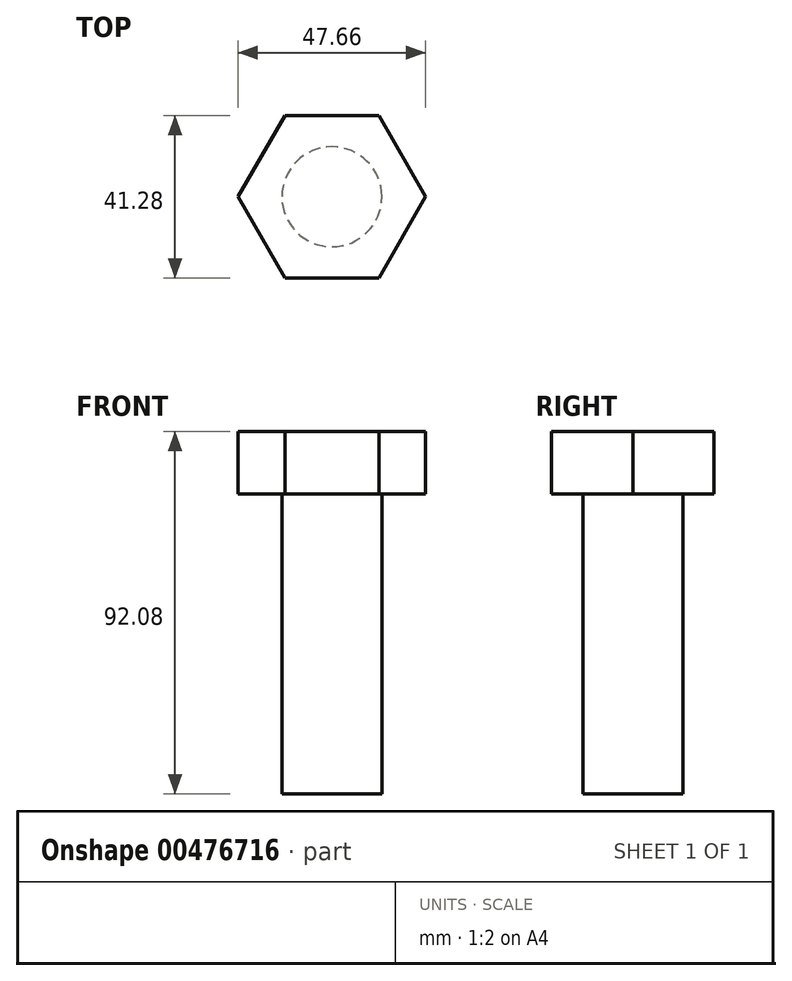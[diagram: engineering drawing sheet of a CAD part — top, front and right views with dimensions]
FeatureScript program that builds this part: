
annotation { "Feature Type Name" : "Feature", "Feature Type Description" : "" }
export const myFeature = defineFeature(function(context is Context, id is Id, definition is map)
    precondition{}
    {
        {
            var Q0;
            Q0=qCreatedBy(makeId("Top.planeOp"),FACE);
            var sketch = newSketch(context, id + "F0", { "sketchPlane" : qUnion([Q0])});
            skCircle(sketch, "E0", {"center": v(0, 0) * mm, "radius": 12.7 * mm});
            skSolve(sketch);
        }
        {
            var Q0;
            Q0=makeQuery(id+"F0.imprint","IMPRINT",FACE,{"disambiguationData":[TD([[makeQuery(id+"F0.imprint","IMPRINT",EDGE,{"derivedFrom":sQuery(id+"F0.wireOp",EDGE,"E0")}),1.0]])]});
            var Q1;
            Q1 = qSketchRegion(id + "F2", true);
            extrude(context, id + "F1", {"entities" : qUnion([Q0, Q1]), "oppositeDirection" : true, "depth" : 38.1 * mm, "hasSecondDirection" : true, "secondDirectionOppositeDirection" : false, "secondDirectionDepth" : 38.1 * mm});
        }
        {
            var Q0;
            Q0=makeQuery(id+"F1.opExtrude","CAP_FACE",FACE,{"disambiguationData":[OSD([sQuery(id+"F0.wireOp",EDGE,"E0")])],"isStart":true});
            var sketch = newSketch(context, id + "F2", { "sketchPlane" : qUnion([Q0])});
            skCircle(sketch, "E1.cCircle", {"center": v(0, 0) * mm, "radius": 20.64 * mm, "construction": true});
            skLineSegment(sketch, "E1.0", {"start": v(-11.92, 20.64) * mm, "end": v(11.92, 20.64) * mm});
            skLineSegment(sketch, "E1.1", {"start": v(11.92, 20.64) * mm, "end": v(23.83, 0) * mm});
            skLineSegment(sketch, "E1.2", {"start": v(23.83, 0) * mm, "end": v(11.92, -20.64) * mm});
            skLineSegment(sketch, "E1.3", {"start": v(11.92, -20.64) * mm, "end": v(-11.92, -20.64) * mm});
            skLineSegment(sketch, "E1.4", {"start": v(-11.92, -20.64) * mm, "end": v(-23.83, 0) * mm});
            skLineSegment(sketch, "E1.5", {"start": v(-23.83, 0) * mm, "end": v(-11.92, 20.64) * mm});
            skPoint(sketch, "E1.0.midPoint", {"position": v(0, 20.64) * mm});
            skSolve(sketch);
        }
        {
            var Q0;
            Q0 = qSketchRegion(id + "F2", true);
            extrude(context, id + "F3", {"entities" : qUnion([Q0]), "operationType" : NewBodyOperationType.ADD, "depth" : 15.88 * mm});
        }
    });
